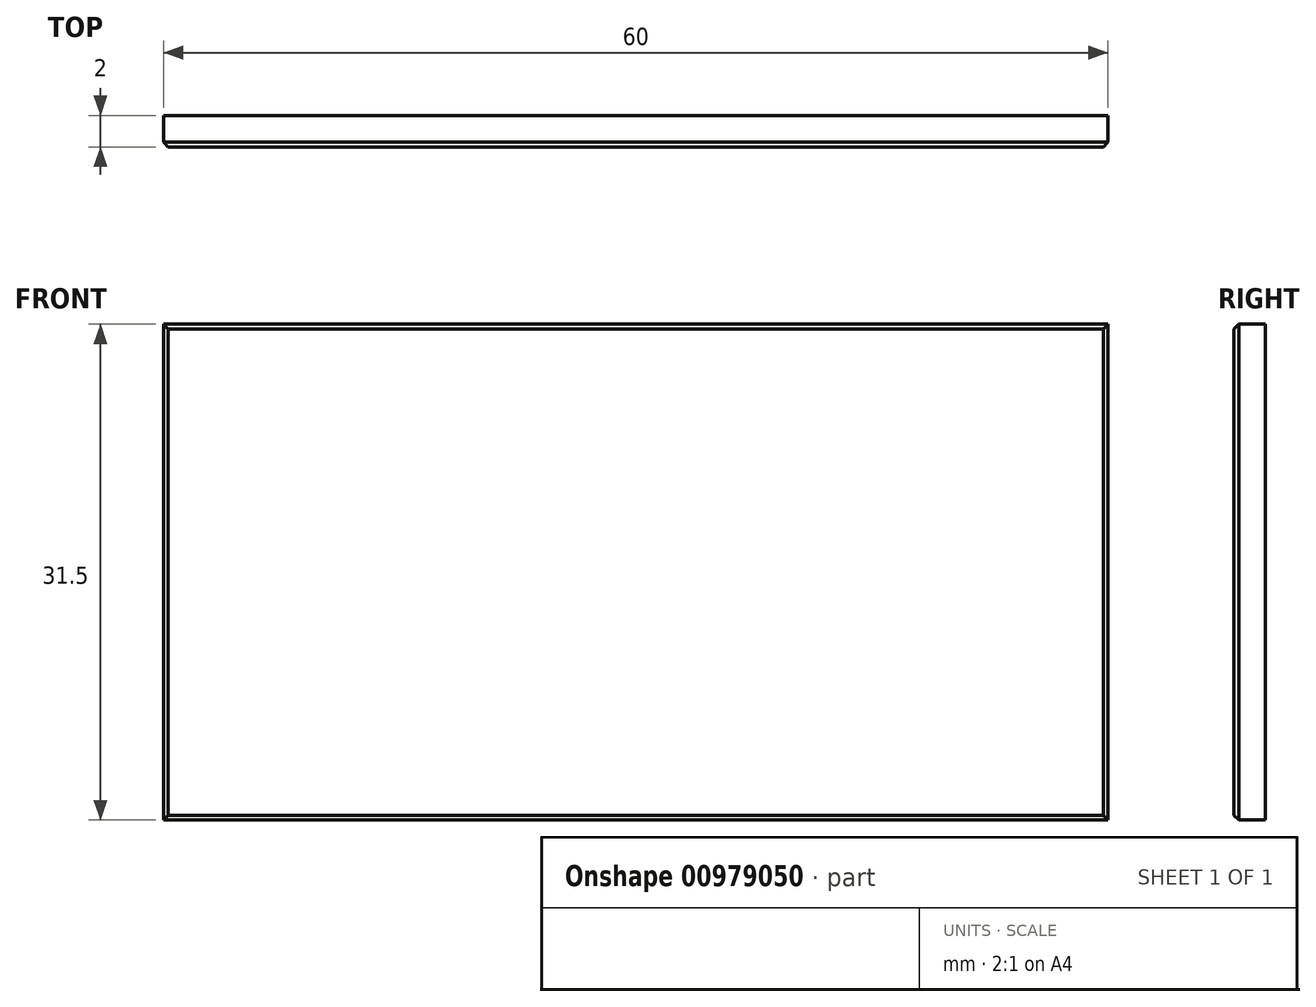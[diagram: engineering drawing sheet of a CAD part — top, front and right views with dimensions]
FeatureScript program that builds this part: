
annotation { "Feature Type Name" : "Feature", "Feature Type Description" : "" }
export const myFeature = defineFeature(function(context is Context, id is Id, definition is map)
    precondition{}
    {
        {
            var Q0;
            Q0=qCreatedBy(makeId("Front.planeOp"),FACE);
            var sketch = newSketch(context, id + "F0", { "sketchPlane" : qUnion([Q0])});
            skLineSegment(sketch, "E0.bottom", {"start": v(-30, 31.5) * mm, "end": v(30, 31.5) * mm});
            skLineSegment(sketch, "E0.top", {"start": v(-30, 0) * mm, "end": v(30, 0) * mm});
            skLineSegment(sketch, "E0.left", {"start": v(-30, 31.5) * mm, "end": v(-30, 0) * mm});
            skLineSegment(sketch, "E0.right", {"start": v(30, 31.5) * mm, "end": v(30, 0) * mm});
            skSolve(sketch);
        }
        {
            var Q0;
            Q0=makeQuery(id+"F0.imprint","IMPRINT",FACE,{"disambiguationData":[TD([[makeQuery(id+"F0.imprint","IMPRINT",EDGE,{"derivedFrom":sQuery(id+"F0.wireOp",EDGE,"E0.bottom")}),-1.0]])]});
            extrude(context, id + "F1", {"entities" : qUnion([Q0]), "depth" : 2 * mm, "offsetDistance" : 25 * mm});
        }
        {
            var Q0;
            Q0=makeQuery(id+"F1.opExtrude","CAP_EDGE",EDGE,{"disambiguationData":[OSD([sQuery(id+"F0.wireOp",EDGE,"E0.bottom")])],"isStart":false});
            var Q1;
            Q1=makeQuery(id+"F1.opExtrude","CAP_EDGE",EDGE,{"disambiguationData":[OSD([sQuery(id+"F0.wireOp",EDGE,"E0.left")])],"isStart":false});
            var Q2;
            Q2=makeQuery(id+"F1.opExtrude","CAP_EDGE",EDGE,{"disambiguationData":[OSD([sQuery(id+"F0.wireOp",EDGE,"E0.right")])],"isStart":false});
            var Q3;
            Q3=makeQuery(id+"F1.opExtrude","CAP_EDGE",EDGE,{"disambiguationData":[OSD([sQuery(id+"F0.wireOp",EDGE,"E0.top")])],"isStart":false});
            chamfer(context, id + "F2", {"entities" : qUnion([Q0, Q1, Q2, Q3]), "width" : 0.3 * mm, "tangentPropagation" : true});
        }
    });
